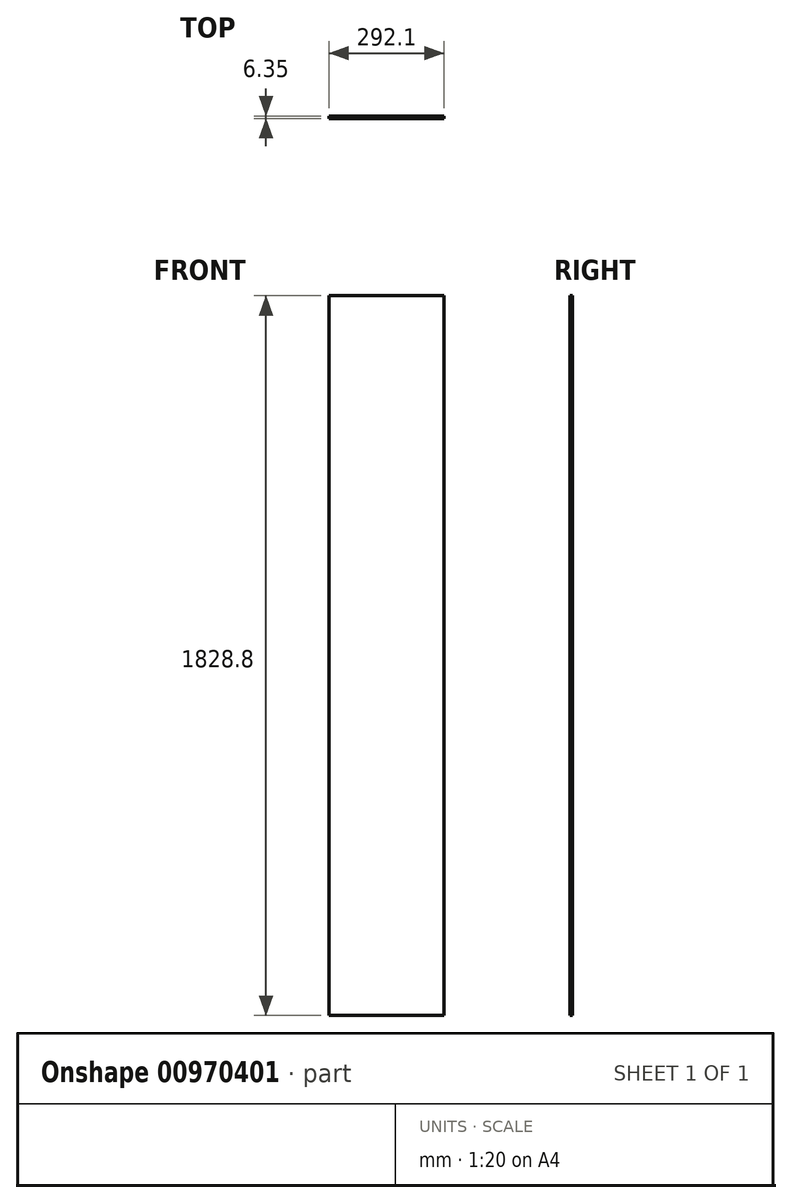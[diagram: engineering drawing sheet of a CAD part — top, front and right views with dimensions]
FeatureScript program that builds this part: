
annotation { "Feature Type Name" : "Feature", "Feature Type Description" : "" }
export const myFeature = defineFeature(function(context is Context, id is Id, definition is map)
    precondition{}
    {
        {
            var Q0;
            Q0=qCreatedBy(makeId("Front.planeOp"),FACE);
            var sketch = newSketch(context, id + "F0", { "sketchPlane" : qUnion([Q0])});
            skLineSegment(sketch, "E0.bottom", {"start": v(292.1, 0) * mm, "end": v(0, 0) * mm});
            skLineSegment(sketch, "E0.top", {"start": v(292.1, -1828.8) * mm, "end": v(0, -1828.8) * mm});
            skLineSegment(sketch, "E0.left", {"start": v(292.1, 0) * mm, "end": v(292.1, -1828.8) * mm});
            skLineSegment(sketch, "E0.right", {"start": v(0, 0) * mm, "end": v(0, -1828.8) * mm});
            skSolve(sketch);
        }
        {
            var Q0;
            Q0=makeQuery(id+"F0.imprint","IMPRINT",FACE,{"disambiguationData":[TD([[makeQuery(id+"F0.imprint","IMPRINT",EDGE,{"derivedFrom":sQuery(id+"F0.wireOp",EDGE,"E0.bottom")}),1.0]])]});
            extrude(context, id + "F1", {"entities" : qUnion([Q0]), "depth" : 6.35 * mm, "offsetDistance" : 25.4 * mm});
        }
    });
